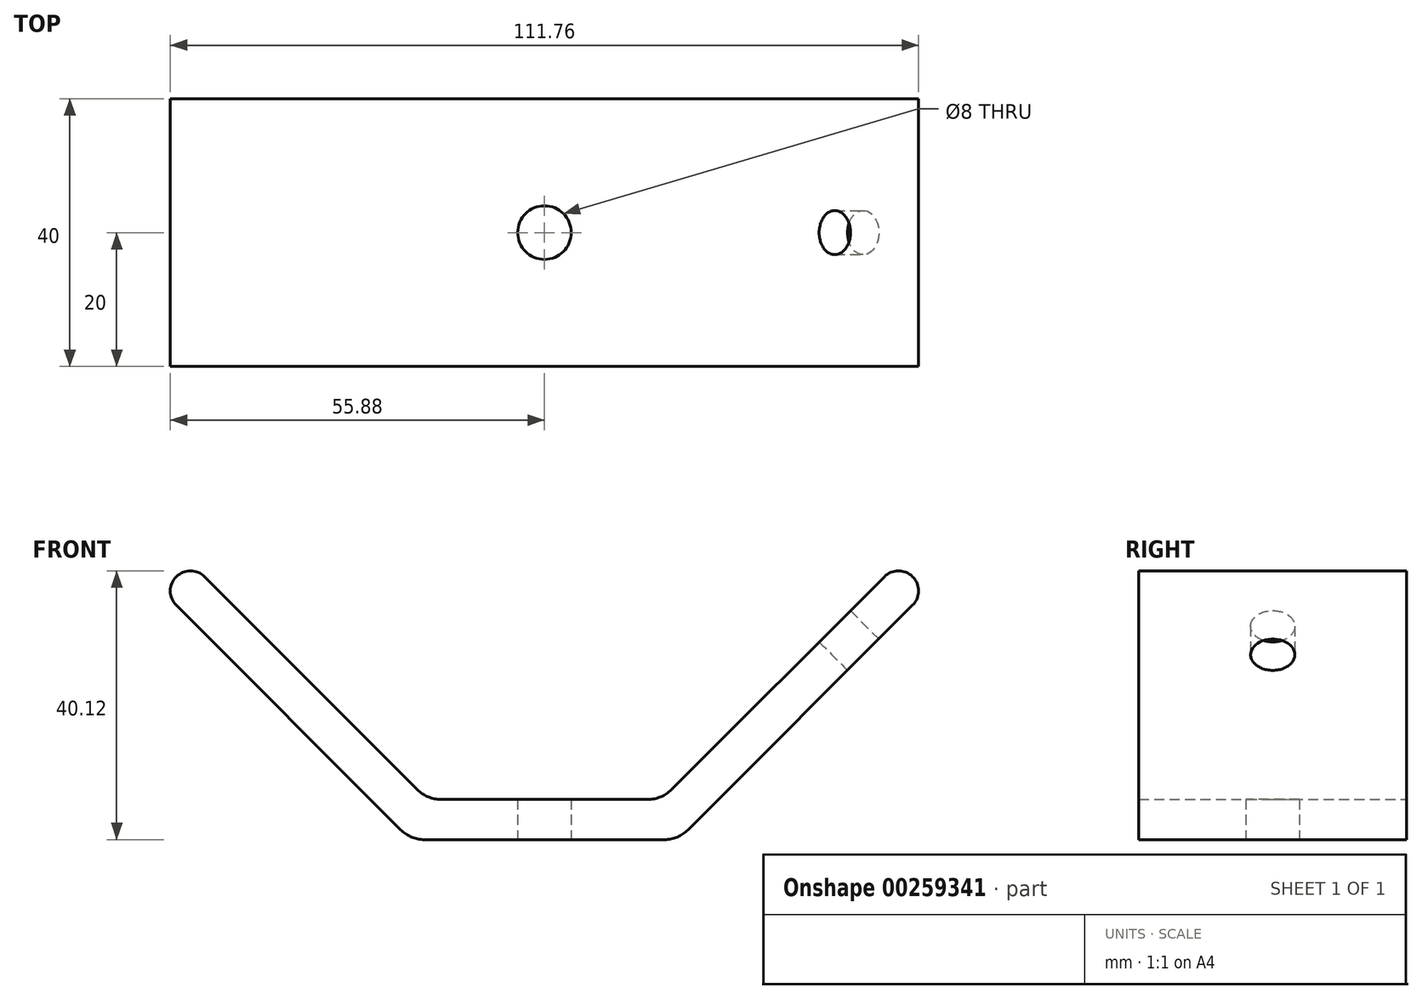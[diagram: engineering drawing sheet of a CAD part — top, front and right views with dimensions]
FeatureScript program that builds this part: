
annotation { "Feature Type Name" : "Feature", "Feature Type Description" : "" }
export const myFeature = defineFeature(function(context is Context, id is Id, definition is map)
    precondition{}
    {
        {
            var Q0;
            Q0=qCreatedBy(makeId("Front.planeOp"),FACE);
            var sketch = newSketch(context, id + "F0", { "sketchPlane" : qUnion([Q0])});
            skLineSegment(sketch, "E0", {"start": v(0, 0) * mm, "end": v(17.93, 0) * mm});
            skLineSegment(sketch, "E1", {"start": v(21.46, 1.46) * mm, "end": v(55, 35) * mm});
            skLineSegment(sketch, "E2.0", {"start": v(18.98, 7.46) * mm, "end": v(50.76, 39.24) * mm});
            skLineSegment(sketch, "E2.1", {"start": v(0, 6) * mm, "end": v(15.44, 6) * mm});
            skArc(sketch, "E3", {"start": v(55, 35) * mm, "mid": v(55, 39.24) * mm, "end": v(50.76, 39.24) * mm});
            skPoint(sketch, "E4.visualSharp", {"position": v(20, 0) * mm});
            skArc(sketch, "E4.filletArc", {"start": v(17.93, 0) * mm, "mid": v(19.84, 0.38) * mm, "end": v(21.46, 1.46) * mm});
            skPoint(sketch, "E5.visualSharp", {"position": v(17.51, 6) * mm});
            skArc(sketch, "E5.filletArc", {"start": v(15.44, 6) * mm, "mid": v(17.36, 6.38) * mm, "end": v(18.98, 7.46) * mm});
            skArc(sketch, "E6.MirrorCS", {"start": v(-15.44, 6) * mm, "mid": v(-17.36, 6.38) * mm, "end": v(-18.98, 7.46) * mm});
            skPoint(sketch, "E7.MirrorP", {"position": v(-20, 0) * mm});
            skLineSegment(sketch, "E8.MirrorCS", {"start": v(0, 6) * mm, "end": v(-15.44, 6) * mm});
            skPoint(sketch, "E9.MirrorP", {"position": v(-17.51, 6) * mm});
            skLineSegment(sketch, "E10.MirrorCS", {"start": v(0, 0) * mm, "end": v(-17.93, 0) * mm});
            skLineSegment(sketch, "E11.MirrorCS", {"start": v(-21.46, 1.46) * mm, "end": v(-55, 35) * mm});
            skArc(sketch, "E12.MirrorCS", {"start": v(-17.93, 0) * mm, "mid": v(-19.84, 0.38) * mm, "end": v(-21.46, 1.46) * mm});
            skLineSegment(sketch, "E13.MirrorCS", {"start": v(-18.98, 7.46) * mm, "end": v(-50.76, 39.24) * mm});
            skArc(sketch, "E14.MirrorCS", {"start": v(-55, 35) * mm, "mid": v(-55, 39.24) * mm, "end": v(-50.76, 39.24) * mm});
            skLineSegment(sketch, "E15", {"start": v(0, 0) * mm, "end": v(0, 17.64) * mm, "construction": true});
            skLineSegment(sketch, "E16", {"start": v(0, 0) * mm, "end": v(0, -13.06) * mm, "construction": true});
            skLineSegment(sketch, "E17", {"start": v(47.6, 27.6) * mm, "end": v(39.72, 35.49) * mm, "construction": true});
            skSolve(sketch);
        }
        {
            var Q0;
            Q0=makeQuery(id+"F0.imprint","IMPRINT",FACE,{"disambiguationData":[TD([[makeQuery(id+"F0.imprint","IMPRINT",EDGE,{"derivedFrom":sQuery(id+"F0.wireOp",EDGE,"E0")}),1.0]])]});
            extrude(context, id + "F1", {"entities" : qUnion([Q0]), "endBound" : BoundingType.SYMMETRIC, "depth" : 40 * mm});
        }
        {
            var Q0;
            Q0=qCreatedBy(makeId("Top.planeOp"),FACE);
            var sketch = newSketch(context, id + "F2", { "sketchPlane" : qUnion([Q0])});
            skCircle(sketch, "E18", {"center": v(0, 0) * mm, "radius": 4 * mm});
            skSolve(sketch);
        }
        {
            var Q0;
            Q0=makeQuery(id+"F2.imprint","IMPRINT",FACE,{"disambiguationData":[TD([[makeQuery(id+"F2.imprint","IMPRINT",EDGE,{"derivedFrom":sQuery(id+"F2.wireOp",EDGE,"E18")}),1.0]])]});
            extrude(context, id + "F3", {"entities" : qUnion([Q0]), "operationType" : NewBodyOperationType.REMOVE, "endBound" : BoundingType.THROUGH_ALL, "depth" : 25 * mm});
        }
        {
            var Q0;
            Q0=makeQuery(id+"F1.opExtrude","SWEPT_FACE",FACE,{"disambiguationData":[OSD([sQuery(id+"F0.wireOp",EDGE,"E1")])]});
            cPlane(context, id + "F4", {"entities" : qUnion([Q0]), "cplaneType" : CPlaneType.OFFSET, "offset" : 0 * mm, "width" : 150 * mm, "height" : 150 * mm});
        }
        {
            var Q0;
            Q0=qCreatedBy(id+"F4.planeOp",FACE);
            var sketch = newSketch(context, id + "F5", { "sketchPlane" : qUnion([Q0])});
            skCircle(sketch, "E19", {"center": v(0, 53.18) * mm, "radius": 3 * mm, "construction": true});
            skLineSegment(sketch, "E20", {"start": v(0, 53.18) * mm, "end": v(4.57, 55.48) * mm});
            skLineSegment(sketch, "E21", {"start": v(0, 53.18) * mm, "end": v(2, 50.15) * mm});
            skSolve(sketch);
        }
        {
            var Q0;
            Q0=sQuery(id+"F5.wireOp",VERTEX,"E19.center");
            var Q1;
            Q1=makeQuery(id+"F1.opExtrude","SWEPT_BODY",BODY,{"disambiguationData":[OSD([sQuery(id+"F0.wireOp",EDGE,"E0"),sQuery(id+"F0.wireOp",EDGE,"E1"),sQuery(id+"F0.wireOp",EDGE,"E2.0"),sQuery(id+"F0.wireOp",EDGE,"E2.1"),sQuery(id+"F0.wireOp",EDGE,"E3"),sQuery(id+"F0.wireOp",EDGE,"E4.filletArc"),sQuery(id+"F0.wireOp",EDGE,"E5.filletArc"),sQuery(id+"F0.wireOp",EDGE,"E6.MirrorCS"),sQuery(id+"F0.wireOp",EDGE,"E8.MirrorCS"),sQuery(id+"F0.wireOp",EDGE,"E10.MirrorCS"),sQuery(id+"F0.wireOp",EDGE,"E11.MirrorCS"),sQuery(id+"F0.wireOp",EDGE,"E12.MirrorCS"),sQuery(id+"F0.wireOp",EDGE,"E13.MirrorCS"),sQuery(id+"F0.wireOp",EDGE,"E14.MirrorCS")])]});
            hole(context, id + "F6", {"style" : HoleStyle.SIMPLE, "endStyle" : HoleEndStyle.THROUGH, "standardTappedOrClearance" : lookupTablePath({ "standard" : "ISO", "fit" : "Normal", "size" : "M6", "type" : "Clearance" }), "standardBlindInLast" : lookupTablePath({ "fit" : "Standard", "standard" : "ISO", "size" : "M6", "type" : "Clearance" }), "holeDiameter" : 6.6 * mm, "tappedDepth" : 12 * mm, "tapClearance" : 3, "locations" : qUnion([Q0]), "scope" : qUnion([Q1])});
        }
    });
